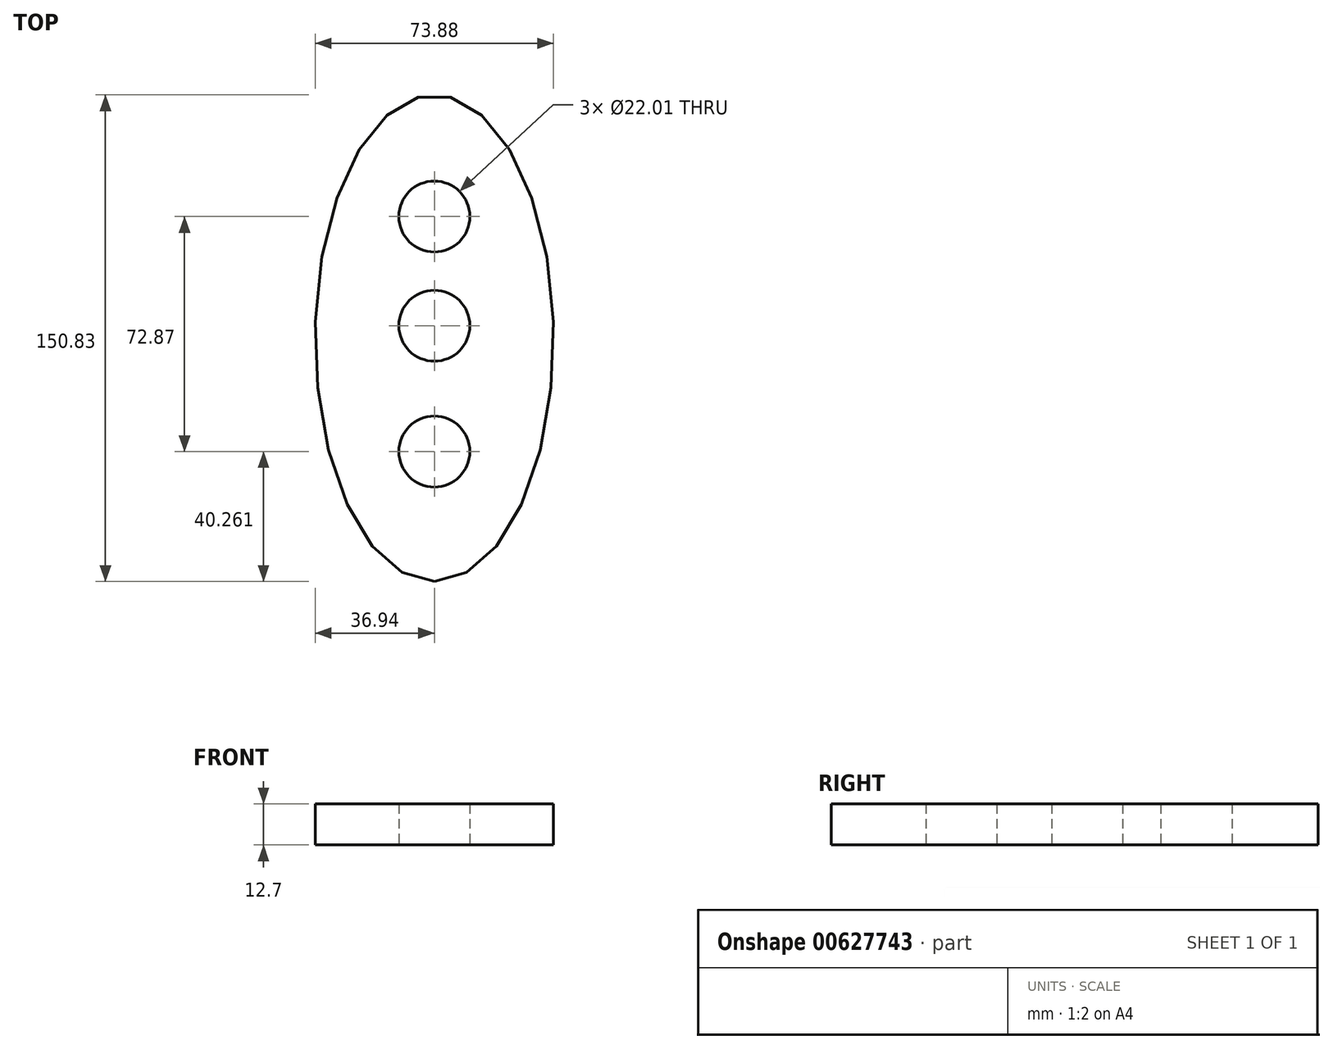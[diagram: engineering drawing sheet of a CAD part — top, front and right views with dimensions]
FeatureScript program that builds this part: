
annotation { "Feature Type Name" : "Feature", "Feature Type Description" : "" }
export const myFeature = defineFeature(function(context is Context, id is Id, definition is map)
    precondition{}
    {
        {
            var Q0;
            Q0=qCreatedBy(makeId("Top.planeOp"),FACE);
            var sketch = newSketch(context, id + "F0", { "sketchPlane" : qUnion([Q0])});
            skEllipse(sketch, "E0", {"center": v(0, 75.42) * mm, "majorRadius": 75.42 * mm, "minorRadius": 36.94 * mm, "majorAxis": v(0, -1)});
            skSolve(sketch);
        }
        {
            var Q0;
            Q0=makeQuery(id+"F0.imprint","IMPRINT",FACE,{"disambiguationData":[TD([[makeQuery(id+"F0.imprint","IMPRINT",EDGE,{"derivedFrom":sQuery(id+"F0.wireOp",EDGE,"E0")}),1.0]])]});
            var sketch = newSketch(context, id + "F1", { "sketchPlane" : qUnion([Q0])});
            skSolve(sketch);
        }
        {
            var Q0;
            Q0=makeQuery(id+"F0.imprint","IMPRINT",FACE,{"disambiguationData":[TD([[makeQuery(id+"F0.imprint","IMPRINT",EDGE,{"derivedFrom":sQuery(id+"F0.wireOp",EDGE,"E0")}),1.0]])]});
            extrude(context, id + "F2", {"entities" : qUnion([Q0]), "depth" : 12.7 * mm, "offsetDistance" : 25.4 * mm});
        }
        {
            var Q0;
            Q0=makeQuery(id+"F1.imprint","IMPRINT",FACE,{"disambiguationData":[TD([[makeQuery(id+"F1.imprint","IMPRINT",EDGE,{"derivedFrom":makeQuery(id+"F0.imprint","IMPRINT",EDGE,{"derivedFrom":sQuery(id+"F0.wireOp",EDGE,"E0")})}),1.0]])]});
            var sketch = newSketch(context, id + "F3", { "sketchPlane" : qUnion([Q0])});
            skPoint(sketch, "E1", {"position": v(0, 40.26) * mm});
            skPoint(sketch, "E2", {"position": v(0, 113.13) * mm});
            skPoint(sketch, "E3", {"position": v(0, 79.3) * mm});
            skPoint(sketch, "E4", {"position": v(-11.04, 204.7) * mm});
            skSolve(sketch);
        }
        {
            var Q0;
            Q0=sQuery(id+"F3.wireOp",VERTEX,"E1");
            var Q1;
            Q1=sQuery(id+"F3.wireOp",VERTEX,"E3");
            var Q2;
            Q2=sQuery(id+"F3.wireOp",VERTEX,"E2");
            var Q3;
            Q3=makeQuery(id+"F2.opExtrude","SWEPT_BODY",BODY,{"disambiguationData":[OSD([sQuery(id+"F0.wireOp",EDGE,"E0")])]});
            hole(context, id + "F4", {"style" : HoleStyle.SIMPLE, "endStyle" : HoleEndStyle.THROUGH, "oppositeDirection" : true, "holeDiameter" : 22.01 * mm, "majorDiameter" : 6.35 * mm, "isTappedThrough" : true, "tappedDepth" : 12.7 * mm, "tapClearance" : 3, "locations" : qUnion([Q0, Q1, Q2]), "scope" : qUnion([Q3])});
        }
    });
